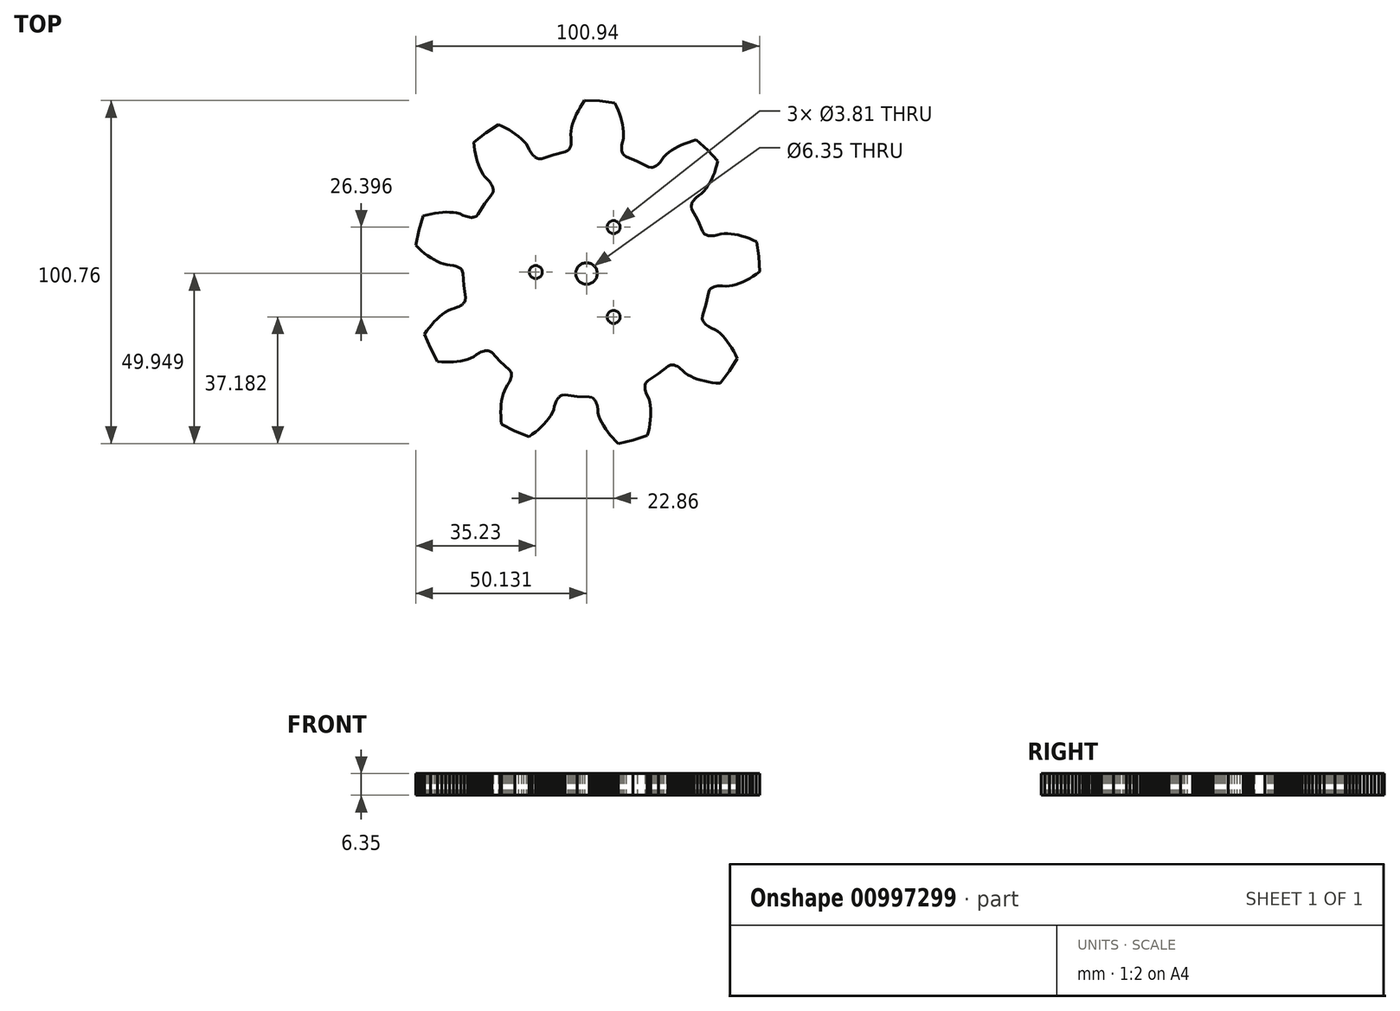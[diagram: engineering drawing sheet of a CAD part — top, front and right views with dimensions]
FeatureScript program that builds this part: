
annotation { "Feature Type Name" : "Feature", "Feature Type Description" : "" }
export const myFeature = defineFeature(function(context is Context, id is Id, definition is map)
    precondition{}
    {
        {
            var Q0;
            Q0=qCreatedBy(makeId("Top.planeOp"),FACE);
            var sketch = newSketch(context, id + "F0", { "sketchPlane" : qUnion([Q0])});
            skLineSegment(sketch, "E0", {"start": v(-36.57, -0.37) * mm, "end": v(-36.8, 0.44) * mm});
            skLineSegment(sketch, "E1", {"start": v(-36.8, 0.44) * mm, "end": v(-37.04, 0.75) * mm});
            skLineSegment(sketch, "E2", {"start": v(-37.04, 0.75) * mm, "end": v(-37.27, 0.98) * mm});
            skLineSegment(sketch, "E3", {"start": v(-37.27, 0.98) * mm, "end": v(-37.51, 1.17) * mm});
            skLineSegment(sketch, "E4", {"start": v(-37.51, 1.17) * mm, "end": v(-37.75, 1.32) * mm});
            skLineSegment(sketch, "E5", {"start": v(-37.75, 1.32) * mm, "end": v(-37.98, 1.45) * mm});
            skLineSegment(sketch, "E6", {"start": v(-37.98, 1.45) * mm, "end": v(-38.46, 1.66) * mm});
            skLineSegment(sketch, "E7", {"start": v(-38.46, 1.66) * mm, "end": v(-38.94, 1.82) * mm});
            skLineSegment(sketch, "E8", {"start": v(-38.94, 1.82) * mm, "end": v(-39.42, 1.93) * mm});
            skLineSegment(sketch, "E9", {"start": v(-39.42, 1.93) * mm, "end": v(-40.38, 2.07) * mm});
            skLineSegment(sketch, "E10", {"start": v(-40.38, 2.07) * mm, "end": v(-41.35, 2.12) * mm});
            skLineSegment(sketch, "E11", {"start": v(-41.35, 2.12) * mm, "end": v(-42.31, 2.36) * mm});
            skLineSegment(sketch, "E12", {"start": v(-42.31, 2.36) * mm, "end": v(-43.26, 2.7) * mm});
            skLineSegment(sketch, "E13", {"start": v(-43.26, 2.7) * mm, "end": v(-44.2, 3.13) * mm});
            skLineSegment(sketch, "E14", {"start": v(-44.2, 3.13) * mm, "end": v(-45.14, 3.63) * mm});
            skLineSegment(sketch, "E15", {"start": v(-45.14, 3.63) * mm, "end": v(-46.06, 4.2) * mm});
            skLineSegment(sketch, "E16", {"start": v(-46.06, 4.2) * mm, "end": v(-46.97, 4.81) * mm});
            skLineSegment(sketch, "E17", {"start": v(-46.97, 4.81) * mm, "end": v(-47.87, 5.5) * mm});
            skLineSegment(sketch, "E18", {"start": v(-47.87, 5.5) * mm, "end": v(-48.75, 6.23) * mm});
            skLineSegment(sketch, "E19", {"start": v(-48.75, 6.23) * mm, "end": v(-49.62, 7.02) * mm});
            skLineSegment(sketch, "E20", {"start": v(-49.62, 7.02) * mm, "end": v(-50.47, 7.86) * mm});
            skLineSegment(sketch, "E21", {"start": v(-50.47, 7.86) * mm, "end": v(-49.56, 12.2) * mm});
            skLineSegment(sketch, "E22", {"start": v(-49.56, 12.2) * mm, "end": v(-48.26, 16.46) * mm});
            skLineSegment(sketch, "E23", {"start": v(-48.26, 16.46) * mm, "end": v(-47.11, 16.78) * mm});
            skLineSegment(sketch, "E24", {"start": v(-47.11, 16.78) * mm, "end": v(-45.97, 17.06) * mm});
            skLineSegment(sketch, "E25", {"start": v(-45.97, 17.06) * mm, "end": v(-44.84, 17.27) * mm});
            skLineSegment(sketch, "E26", {"start": v(-44.84, 17.27) * mm, "end": v(-43.73, 17.44) * mm});
            skLineSegment(sketch, "E27", {"start": v(-43.73, 17.44) * mm, "end": v(-42.63, 17.54) * mm});
            skLineSegment(sketch, "E28", {"start": v(-42.63, 17.54) * mm, "end": v(-41.55, 17.6) * mm});
            skLineSegment(sketch, "E29", {"start": v(-41.55, 17.6) * mm, "end": v(-40.5, 17.58) * mm});
            skLineSegment(sketch, "E30", {"start": v(-40.5, 17.58) * mm, "end": v(-39.46, 17.5) * mm});
            skLineSegment(sketch, "E31", {"start": v(-39.46, 17.5) * mm, "end": v(-38.46, 17.34) * mm});
            skLineSegment(sketch, "E32", {"start": v(-38.46, 17.34) * mm, "end": v(-37.51, 17.09) * mm});
            skLineSegment(sketch, "E33", {"start": v(-37.51, 17.09) * mm, "end": v(-36.63, 16.67) * mm});
            skLineSegment(sketch, "E34", {"start": v(-36.63, 16.67) * mm, "end": v(-35.72, 16.33) * mm});
            skLineSegment(sketch, "E35", {"start": v(-35.72, 16.33) * mm, "end": v(-35.25, 16.2) * mm});
            skLineSegment(sketch, "E36", {"start": v(-35.25, 16.2) * mm, "end": v(-34.75, 16.1) * mm});
            skLineSegment(sketch, "E37", {"start": v(-34.75, 16.1) * mm, "end": v(-34.23, 16.06) * mm});
            skLineSegment(sketch, "E38", {"start": v(-34.23, 16.06) * mm, "end": v(-33.96, 16.05) * mm});
            skLineSegment(sketch, "E39", {"start": v(-33.96, 16.05) * mm, "end": v(-33.68, 16.08) * mm});
            skLineSegment(sketch, "E40", {"start": v(-33.68, 16.08) * mm, "end": v(-33.39, 16.12) * mm});
            skLineSegment(sketch, "E41", {"start": v(-33.39, 16.12) * mm, "end": v(-33.07, 16.21) * mm});
            skLineSegment(sketch, "E42", {"start": v(-33.07, 16.21) * mm, "end": v(-32.71, 16.38) * mm});
            skLineSegment(sketch, "E43", {"start": v(-32.71, 16.38) * mm, "end": v(-32.12, 16.97) * mm});
            skLineSegment(sketch, "E44", {"start": v(-32.12, 16.97) * mm, "end": v(-30.24, 20.04) * mm});
            skLineSegment(sketch, "E45", {"start": v(-30.24, 20.04) * mm, "end": v(-28.05, 22.9) * mm});
            skLineSegment(sketch, "E46", {"start": v(-28.05, 22.9) * mm, "end": v(-27.72, 23.67) * mm});
            skLineSegment(sketch, "E47", {"start": v(-27.72, 23.67) * mm, "end": v(-27.7, 24.07) * mm});
            skLineSegment(sketch, "E48", {"start": v(-27.7, 24.07) * mm, "end": v(-27.72, 24.4) * mm});
            skLineSegment(sketch, "E49", {"start": v(-27.72, 24.4) * mm, "end": v(-27.79, 24.69) * mm});
            skLineSegment(sketch, "E50", {"start": v(-27.79, 24.69) * mm, "end": v(-27.87, 24.96) * mm});
            skLineSegment(sketch, "E51", {"start": v(-27.87, 24.96) * mm, "end": v(-27.97, 25.2) * mm});
            skLineSegment(sketch, "E52", {"start": v(-27.97, 25.2) * mm, "end": v(-28.2, 25.67) * mm});
            skLineSegment(sketch, "E53", {"start": v(-28.2, 25.67) * mm, "end": v(-28.46, 26.1) * mm});
            skLineSegment(sketch, "E54", {"start": v(-28.46, 26.1) * mm, "end": v(-28.76, 26.5) * mm});
            skLineSegment(sketch, "E55", {"start": v(-28.76, 26.5) * mm, "end": v(-29.4, 27.22) * mm});
            skLineSegment(sketch, "E56", {"start": v(-29.4, 27.22) * mm, "end": v(-30.12, 27.89) * mm});
            skLineSegment(sketch, "E57", {"start": v(-30.12, 27.89) * mm, "end": v(-30.7, 28.69) * mm});
            skLineSegment(sketch, "E58", {"start": v(-30.7, 28.69) * mm, "end": v(-31.2, 29.56) * mm});
            skLineSegment(sketch, "E59", {"start": v(-31.2, 29.56) * mm, "end": v(-31.65, 30.5) * mm});
            skLineSegment(sketch, "E60", {"start": v(-31.65, 30.5) * mm, "end": v(-32.05, 31.47) * mm});
            skLineSegment(sketch, "E61", {"start": v(-32.05, 31.47) * mm, "end": v(-32.4, 32.5) * mm});
            skLineSegment(sketch, "E62", {"start": v(-32.4, 32.5) * mm, "end": v(-32.69, 33.56) * mm});
            skLineSegment(sketch, "E63", {"start": v(-32.69, 33.56) * mm, "end": v(-32.94, 34.66) * mm});
            skLineSegment(sketch, "E64", {"start": v(-32.94, 34.66) * mm, "end": v(-33.14, 35.8) * mm});
            skLineSegment(sketch, "E65", {"start": v(-33.14, 35.8) * mm, "end": v(-33.3, 36.95) * mm});
            skLineSegment(sketch, "E66", {"start": v(-33.3, 36.95) * mm, "end": v(-33.41, 38.14) * mm});
            skLineSegment(sketch, "E67", {"start": v(-33.41, 38.14) * mm, "end": v(-29.92, 40.88) * mm});
            skLineSegment(sketch, "E68", {"start": v(-29.92, 40.88) * mm, "end": v(-26.2, 43.31) * mm});
            skLineSegment(sketch, "E69", {"start": v(-26.2, 43.31) * mm, "end": v(-25.1, 42.82) * mm});
            skLineSegment(sketch, "E70", {"start": v(-25.1, 42.82) * mm, "end": v(-24.06, 42.3) * mm});
            skLineSegment(sketch, "E71", {"start": v(-24.06, 42.3) * mm, "end": v(-23.05, 41.74) * mm});
            skLineSegment(sketch, "E72", {"start": v(-23.05, 41.74) * mm, "end": v(-22.1, 41.15) * mm});
            skLineSegment(sketch, "E73", {"start": v(-22.1, 41.15) * mm, "end": v(-21.18, 40.52) * mm});
            skLineSegment(sketch, "E74", {"start": v(-21.18, 40.52) * mm, "end": v(-20.32, 39.87) * mm});
            skLineSegment(sketch, "E75", {"start": v(-20.32, 39.87) * mm, "end": v(-19.52, 39.18) * mm});
            skLineSegment(sketch, "E76", {"start": v(-19.52, 39.18) * mm, "end": v(-18.78, 38.45) * mm});
            skLineSegment(sketch, "E77", {"start": v(-18.78, 38.45) * mm, "end": v(-18.12, 37.7) * mm});
            skLineSegment(sketch, "E78", {"start": v(-18.12, 37.7) * mm, "end": v(-17.55, 36.88) * mm});
            skLineSegment(sketch, "E79", {"start": v(-17.55, 36.88) * mm, "end": v(-17.15, 36) * mm});
            skLineSegment(sketch, "E80", {"start": v(-17.15, 36) * mm, "end": v(-16.67, 35.15) * mm});
            skLineSegment(sketch, "E81", {"start": v(-16.67, 35.15) * mm, "end": v(-16.4, 34.74) * mm});
            skLineSegment(sketch, "E82", {"start": v(-16.4, 34.74) * mm, "end": v(-16.07, 34.35) * mm});
            skLineSegment(sketch, "E83", {"start": v(-16.07, 34.35) * mm, "end": v(-15.7, 33.99) * mm});
            skLineSegment(sketch, "E84", {"start": v(-15.7, 33.99) * mm, "end": v(-15.5, 33.81) * mm});
            skLineSegment(sketch, "E85", {"start": v(-15.5, 33.81) * mm, "end": v(-15.27, 33.65) * mm});
            skLineSegment(sketch, "E86", {"start": v(-15.27, 33.65) * mm, "end": v(-15.02, 33.5) * mm});
            skLineSegment(sketch, "E87", {"start": v(-15.02, 33.5) * mm, "end": v(-14.72, 33.36) * mm});
            skLineSegment(sketch, "E88", {"start": v(-14.72, 33.36) * mm, "end": v(-14.34, 33.25) * mm});
            skLineSegment(sketch, "E89", {"start": v(-14.34, 33.25) * mm, "end": v(-13.5, 33.33) * mm});
            skLineSegment(sketch, "E90", {"start": v(-13.5, 33.33) * mm, "end": v(-10.08, 34.47) * mm});
            skLineSegment(sketch, "E91", {"start": v(-10.08, 34.47) * mm, "end": v(-6.57, 35.26) * mm});
            skLineSegment(sketch, "E92", {"start": v(-6.57, 35.26) * mm, "end": v(-5.82, 35.63) * mm});
            skLineSegment(sketch, "E93", {"start": v(-5.82, 35.63) * mm, "end": v(-5.55, 35.92) * mm});
            skLineSegment(sketch, "E94", {"start": v(-5.55, 35.92) * mm, "end": v(-5.36, 36.19) * mm});
            skLineSegment(sketch, "E95", {"start": v(-5.36, 36.19) * mm, "end": v(-5.22, 36.45) * mm});
            skLineSegment(sketch, "E96", {"start": v(-5.22, 36.45) * mm, "end": v(-5.1, 36.71) * mm});
            skLineSegment(sketch, "E97", {"start": v(-5.1, 36.71) * mm, "end": v(-5.02, 36.97) * mm});
            skLineSegment(sketch, "E98", {"start": v(-5.02, 36.97) * mm, "end": v(-4.9, 37.47) * mm});
            skLineSegment(sketch, "E99", {"start": v(-4.9, 37.47) * mm, "end": v(-4.83, 37.97) * mm});
            skLineSegment(sketch, "E100", {"start": v(-4.83, 37.97) * mm, "end": v(-4.8, 38.46) * mm});
            skLineSegment(sketch, "E101", {"start": v(-4.8, 38.46) * mm, "end": v(-4.83, 39.44) * mm});
            skLineSegment(sketch, "E102", {"start": v(-4.83, 39.44) * mm, "end": v(-4.95, 40.4) * mm});
            skLineSegment(sketch, "E103", {"start": v(-4.95, 40.4) * mm, "end": v(-4.88, 41.39) * mm});
            skLineSegment(sketch, "E104", {"start": v(-4.88, 41.39) * mm, "end": v(-4.7, 42.38) * mm});
            skLineSegment(sketch, "E105", {"start": v(-4.7, 42.38) * mm, "end": v(-4.45, 43.39) * mm});
            skLineSegment(sketch, "E106", {"start": v(-4.45, 43.39) * mm, "end": v(-4.12, 44.4) * mm});
            skLineSegment(sketch, "E107", {"start": v(-4.12, 44.4) * mm, "end": v(-3.73, 45.4) * mm});
            skLineSegment(sketch, "E108", {"start": v(-3.73, 45.4) * mm, "end": v(-3.27, 46.4) * mm});
            skLineSegment(sketch, "E109", {"start": v(-3.27, 46.4) * mm, "end": v(-2.76, 47.4) * mm});
            skLineSegment(sketch, "E110", {"start": v(-2.76, 47.4) * mm, "end": v(-2.19, 48.4) * mm});
            skLineSegment(sketch, "E111", {"start": v(-2.19, 48.4) * mm, "end": v(-1.56, 49.4) * mm});
            skLineSegment(sketch, "E112", {"start": v(-1.56, 49.4) * mm, "end": v(-0.88, 50.38) * mm});
            skLineSegment(sketch, "E113", {"start": v(-0.88, 50.38) * mm, "end": v(3.56, 50.23) * mm});
            skLineSegment(sketch, "E114", {"start": v(3.56, 50.23) * mm, "end": v(7.97, 49.7) * mm});
            skLineSegment(sketch, "E115", {"start": v(7.97, 49.7) * mm, "end": v(8.5, 48.62) * mm});
            skLineSegment(sketch, "E116", {"start": v(8.5, 48.62) * mm, "end": v(8.96, 47.55) * mm});
            skLineSegment(sketch, "E117", {"start": v(8.96, 47.55) * mm, "end": v(9.37, 46.47) * mm});
            skLineSegment(sketch, "E118", {"start": v(9.37, 46.47) * mm, "end": v(9.72, 45.4) * mm});
            skLineSegment(sketch, "E119", {"start": v(9.72, 45.4) * mm, "end": v(10.02, 44.34) * mm});
            skLineSegment(sketch, "E120", {"start": v(10.02, 44.34) * mm, "end": v(10.25, 43.28) * mm});
            skLineSegment(sketch, "E121", {"start": v(10.25, 43.28) * mm, "end": v(10.43, 42.24) * mm});
            skLineSegment(sketch, "E122", {"start": v(10.43, 42.24) * mm, "end": v(10.53, 41.21) * mm});
            skLineSegment(sketch, "E123", {"start": v(10.53, 41.21) * mm, "end": v(10.55, 40.2) * mm});
            skLineSegment(sketch, "E124", {"start": v(10.55, 40.2) * mm, "end": v(10.46, 39.22) * mm});
            skLineSegment(sketch, "E125", {"start": v(10.46, 39.22) * mm, "end": v(10.2, 38.28) * mm});
            skLineSegment(sketch, "E126", {"start": v(10.2, 38.28) * mm, "end": v(10.02, 37.32) * mm});
            skLineSegment(sketch, "E127", {"start": v(10.02, 37.32) * mm, "end": v(9.97, 36.83) * mm});
            skLineSegment(sketch, "E128", {"start": v(9.97, 36.83) * mm, "end": v(9.97, 36.33) * mm});
            skLineSegment(sketch, "E129", {"start": v(9.97, 36.33) * mm, "end": v(10.01, 35.81) * mm});
            skLineSegment(sketch, "E130", {"start": v(10.01, 35.81) * mm, "end": v(10.06, 35.55) * mm});
            skLineSegment(sketch, "E131", {"start": v(10.06, 35.55) * mm, "end": v(10.13, 35.27) * mm});
            skLineSegment(sketch, "E132", {"start": v(10.13, 35.27) * mm, "end": v(10.22, 35) * mm});
            skLineSegment(sketch, "E133", {"start": v(10.22, 35) * mm, "end": v(10.37, 34.7) * mm});
            skLineSegment(sketch, "E134", {"start": v(10.37, 34.7) * mm, "end": v(10.6, 34.37) * mm});
            skLineSegment(sketch, "E135", {"start": v(10.6, 34.37) * mm, "end": v(11.28, 33.9) * mm});
            skLineSegment(sketch, "E136", {"start": v(11.28, 33.9) * mm, "end": v(14.63, 32.57) * mm});
            skLineSegment(sketch, "E137", {"start": v(14.63, 32.57) * mm, "end": v(17.83, 30.92) * mm});
            skLineSegment(sketch, "E138", {"start": v(17.83, 30.92) * mm, "end": v(18.65, 30.72) * mm});
            skLineSegment(sketch, "E139", {"start": v(18.65, 30.72) * mm, "end": v(19.04, 30.76) * mm});
            skLineSegment(sketch, "E140", {"start": v(19.04, 30.76) * mm, "end": v(19.35, 30.85) * mm});
            skLineSegment(sketch, "E141", {"start": v(19.35, 30.85) * mm, "end": v(19.63, 30.96) * mm});
            skLineSegment(sketch, "E142", {"start": v(19.63, 30.96) * mm, "end": v(19.88, 31.09) * mm});
            skLineSegment(sketch, "E143", {"start": v(19.88, 31.09) * mm, "end": v(20.11, 31.23) * mm});
            skLineSegment(sketch, "E144", {"start": v(20.11, 31.23) * mm, "end": v(20.53, 31.54) * mm});
            skLineSegment(sketch, "E145", {"start": v(20.53, 31.54) * mm, "end": v(20.9, 31.87) * mm});
            skLineSegment(sketch, "E146", {"start": v(20.9, 31.87) * mm, "end": v(21.25, 32.23) * mm});
            skLineSegment(sketch, "E147", {"start": v(21.25, 32.23) * mm, "end": v(21.85, 33) * mm});
            skLineSegment(sketch, "E148", {"start": v(21.85, 33) * mm, "end": v(22.38, 33.81) * mm});
            skLineSegment(sketch, "E149", {"start": v(22.38, 33.81) * mm, "end": v(23.06, 34.52) * mm});
            skLineSegment(sketch, "E150", {"start": v(23.06, 34.52) * mm, "end": v(23.84, 35.17) * mm});
            skLineSegment(sketch, "E151", {"start": v(23.84, 35.17) * mm, "end": v(24.68, 35.78) * mm});
            skLineSegment(sketch, "E152", {"start": v(24.68, 35.78) * mm, "end": v(25.58, 36.33) * mm});
            skLineSegment(sketch, "E153", {"start": v(25.58, 36.33) * mm, "end": v(26.52, 36.85) * mm});
            skLineSegment(sketch, "E154", {"start": v(26.52, 36.85) * mm, "end": v(27.52, 37.33) * mm});
            skLineSegment(sketch, "E155", {"start": v(27.52, 37.33) * mm, "end": v(28.56, 37.77) * mm});
            skLineSegment(sketch, "E156", {"start": v(28.56, 37.77) * mm, "end": v(29.64, 38.17) * mm});
            skLineSegment(sketch, "E157", {"start": v(29.64, 38.17) * mm, "end": v(30.75, 38.52) * mm});
            skLineSegment(sketch, "E158", {"start": v(30.75, 38.52) * mm, "end": v(31.9, 38.84) * mm});
            skLineSegment(sketch, "E159", {"start": v(31.9, 38.84) * mm, "end": v(35.21, 35.87) * mm});
            skLineSegment(sketch, "E160", {"start": v(35.21, 35.87) * mm, "end": v(38.25, 32.63) * mm});
            skLineSegment(sketch, "E161", {"start": v(38.25, 32.63) * mm, "end": v(37.96, 31.47) * mm});
            skLineSegment(sketch, "E162", {"start": v(37.96, 31.47) * mm, "end": v(37.62, 30.35) * mm});
            skLineSegment(sketch, "E163", {"start": v(37.62, 30.35) * mm, "end": v(37.25, 29.26) * mm});
            skLineSegment(sketch, "E164", {"start": v(37.25, 29.26) * mm, "end": v(36.83, 28.21) * mm});
            skLineSegment(sketch, "E165", {"start": v(36.83, 28.21) * mm, "end": v(36.37, 27.2) * mm});
            skLineSegment(sketch, "E166", {"start": v(36.37, 27.2) * mm, "end": v(35.88, 26.25) * mm});
            skLineSegment(sketch, "E167", {"start": v(35.88, 26.25) * mm, "end": v(35.34, 25.34) * mm});
            skLineSegment(sketch, "E168", {"start": v(35.34, 25.34) * mm, "end": v(34.75, 24.49) * mm});
            skLineSegment(sketch, "E169", {"start": v(34.75, 24.49) * mm, "end": v(34.12, 23.7) * mm});
            skLineSegment(sketch, "E170", {"start": v(34.12, 23.7) * mm, "end": v(33.42, 23) * mm});
            skLineSegment(sketch, "E171", {"start": v(33.42, 23) * mm, "end": v(32.62, 22.45) * mm});
            skLineSegment(sketch, "E172", {"start": v(32.62, 22.45) * mm, "end": v(31.86, 21.83) * mm});
            skLineSegment(sketch, "E173", {"start": v(31.86, 21.83) * mm, "end": v(31.51, 21.49) * mm});
            skLineSegment(sketch, "E174", {"start": v(31.51, 21.49) * mm, "end": v(31.19, 21.1) * mm});
            skLineSegment(sketch, "E175", {"start": v(31.19, 21.1) * mm, "end": v(30.89, 20.68) * mm});
            skLineSegment(sketch, "E176", {"start": v(30.89, 20.68) * mm, "end": v(30.75, 20.45) * mm});
            skLineSegment(sketch, "E177", {"start": v(30.75, 20.45) * mm, "end": v(30.63, 20.2) * mm});
            skLineSegment(sketch, "E178", {"start": v(30.63, 20.2) * mm, "end": v(30.52, 19.91) * mm});
            skLineSegment(sketch, "E179", {"start": v(30.52, 19.91) * mm, "end": v(30.44, 19.6) * mm});
            skLineSegment(sketch, "E180", {"start": v(30.44, 19.6) * mm, "end": v(30.4, 19.2) * mm});
            skLineSegment(sketch, "E181", {"start": v(30.4, 19.2) * mm, "end": v(30.62, 18.4) * mm});
            skLineSegment(sketch, "E182", {"start": v(30.62, 18.4) * mm, "end": v(32.34, 15.23) * mm});
            skLineSegment(sketch, "E183", {"start": v(32.34, 15.23) * mm, "end": v(33.73, 11.9) * mm});
            skLineSegment(sketch, "E184", {"start": v(33.73, 11.9) * mm, "end": v(34.23, 11.23) * mm});
            skLineSegment(sketch, "E185", {"start": v(34.23, 11.23) * mm, "end": v(34.55, 11) * mm});
            skLineSegment(sketch, "E186", {"start": v(34.55, 11) * mm, "end": v(34.85, 10.87) * mm});
            skLineSegment(sketch, "E187", {"start": v(34.85, 10.87) * mm, "end": v(35.14, 10.78) * mm});
            skLineSegment(sketch, "E188", {"start": v(35.14, 10.78) * mm, "end": v(35.41, 10.72) * mm});
            skLineSegment(sketch, "E189", {"start": v(35.41, 10.72) * mm, "end": v(35.68, 10.68) * mm});
            skLineSegment(sketch, "E190", {"start": v(35.68, 10.68) * mm, "end": v(36.2, 10.64) * mm});
            skLineSegment(sketch, "E191", {"start": v(36.2, 10.64) * mm, "end": v(36.7, 10.66) * mm});
            skLineSegment(sketch, "E192", {"start": v(36.7, 10.66) * mm, "end": v(37.2, 10.72) * mm});
            skLineSegment(sketch, "E193", {"start": v(37.2, 10.72) * mm, "end": v(38.14, 10.92) * mm});
            skLineSegment(sketch, "E194", {"start": v(38.14, 10.92) * mm, "end": v(39.08, 11.2) * mm});
            skLineSegment(sketch, "E195", {"start": v(39.08, 11.2) * mm, "end": v(40.06, 11.3) * mm});
            skLineSegment(sketch, "E196", {"start": v(40.06, 11.3) * mm, "end": v(41.07, 11.3) * mm});
            skLineSegment(sketch, "E197", {"start": v(41.07, 11.3) * mm, "end": v(42.1, 11.22) * mm});
            skLineSegment(sketch, "E198", {"start": v(42.1, 11.22) * mm, "end": v(43.15, 11.08) * mm});
            skLineSegment(sketch, "E199", {"start": v(43.15, 11.08) * mm, "end": v(44.2, 10.86) * mm});
            skLineSegment(sketch, "E200", {"start": v(44.2, 10.86) * mm, "end": v(45.27, 10.59) * mm});
            skLineSegment(sketch, "E201", {"start": v(45.27, 10.59) * mm, "end": v(46.35, 10.26) * mm});
            skLineSegment(sketch, "E202", {"start": v(46.35, 10.26) * mm, "end": v(47.43, 9.87) * mm});
            skLineSegment(sketch, "E203", {"start": v(47.43, 9.87) * mm, "end": v(48.52, 9.42) * mm});
            skLineSegment(sketch, "E204", {"start": v(48.52, 9.42) * mm, "end": v(49.6, 8.93) * mm});
            skLineSegment(sketch, "E205", {"start": v(49.6, 8.93) * mm, "end": v(50.23, 4.53) * mm});
            skLineSegment(sketch, "E206", {"start": v(50.23, 4.53) * mm, "end": v(50.47, 0.1) * mm});
            skLineSegment(sketch, "E207", {"start": v(50.47, 0.1) * mm, "end": v(49.5, -0.6) * mm});
            skLineSegment(sketch, "E208", {"start": v(49.5, -0.6) * mm, "end": v(48.52, -1.26) * mm});
            skLineSegment(sketch, "E209", {"start": v(48.52, -1.26) * mm, "end": v(47.54, -1.85) * mm});
            skLineSegment(sketch, "E210", {"start": v(47.54, -1.85) * mm, "end": v(46.55, -2.38) * mm});
            skLineSegment(sketch, "E211", {"start": v(46.55, -2.38) * mm, "end": v(45.55, -2.86) * mm});
            skLineSegment(sketch, "E212", {"start": v(45.55, -2.86) * mm, "end": v(44.55, -3.27) * mm});
            skLineSegment(sketch, "E213", {"start": v(44.55, -3.27) * mm, "end": v(43.55, -3.62) * mm});
            skLineSegment(sketch, "E214", {"start": v(43.55, -3.62) * mm, "end": v(42.56, -3.9) * mm});
            skLineSegment(sketch, "E215", {"start": v(42.56, -3.9) * mm, "end": v(41.57, -4.1) * mm});
            skLineSegment(sketch, "E216", {"start": v(41.57, -4.1) * mm, "end": v(40.58, -4.18) * mm});
            skLineSegment(sketch, "E217", {"start": v(40.58, -4.18) * mm, "end": v(39.62, -4.09) * mm});
            skLineSegment(sketch, "E218", {"start": v(39.62, -4.09) * mm, "end": v(38.64, -4.08) * mm});
            skLineSegment(sketch, "E219", {"start": v(38.64, -4.08) * mm, "end": v(38.15, -4.12) * mm});
            skLineSegment(sketch, "E220", {"start": v(38.15, -4.12) * mm, "end": v(37.65, -4.2) * mm});
            skLineSegment(sketch, "E221", {"start": v(37.65, -4.2) * mm, "end": v(37.15, -4.33) * mm});
            skLineSegment(sketch, "E222", {"start": v(37.15, -4.33) * mm, "end": v(36.9, -4.42) * mm});
            skLineSegment(sketch, "E223", {"start": v(36.9, -4.42) * mm, "end": v(36.64, -4.54) * mm});
            skLineSegment(sketch, "E224", {"start": v(36.64, -4.54) * mm, "end": v(36.38, -4.68) * mm});
            skLineSegment(sketch, "E225", {"start": v(36.38, -4.68) * mm, "end": v(36.11, -4.88) * mm});
            skLineSegment(sketch, "E226", {"start": v(36.11, -4.88) * mm, "end": v(35.83, -5.15) * mm});
            skLineSegment(sketch, "E227", {"start": v(35.83, -5.15) * mm, "end": v(35.48, -5.91) * mm});
            skLineSegment(sketch, "E228", {"start": v(35.48, -5.91) * mm, "end": v(34.76, -9.44) * mm});
            skLineSegment(sketch, "E229", {"start": v(34.76, -9.44) * mm, "end": v(33.69, -12.88) * mm});
            skLineSegment(sketch, "E230", {"start": v(33.69, -12.88) * mm, "end": v(33.63, -13.72) * mm});
            skLineSegment(sketch, "E231", {"start": v(33.63, -13.72) * mm, "end": v(33.74, -14.1) * mm});
            skLineSegment(sketch, "E232", {"start": v(33.74, -14.1) * mm, "end": v(33.89, -14.4) * mm});
            skLineSegment(sketch, "E233", {"start": v(33.89, -14.4) * mm, "end": v(34.04, -14.65) * mm});
            skLineSegment(sketch, "E234", {"start": v(34.04, -14.65) * mm, "end": v(34.21, -14.87) * mm});
            skLineSegment(sketch, "E235", {"start": v(34.21, -14.87) * mm, "end": v(34.4, -15.07) * mm});
            skLineSegment(sketch, "E236", {"start": v(34.4, -15.07) * mm, "end": v(34.77, -15.43) * mm});
            skLineSegment(sketch, "E237", {"start": v(34.77, -15.43) * mm, "end": v(35.16, -15.74) * mm});
            skLineSegment(sketch, "E238", {"start": v(35.16, -15.74) * mm, "end": v(35.57, -16.02) * mm});
            skLineSegment(sketch, "E239", {"start": v(35.57, -16.02) * mm, "end": v(36.44, -16.47) * mm});
            skLineSegment(sketch, "E240", {"start": v(36.44, -16.47) * mm, "end": v(37.33, -16.86) * mm});
            skLineSegment(sketch, "E241", {"start": v(37.33, -16.86) * mm, "end": v(38.15, -17.4) * mm});
            skLineSegment(sketch, "E242", {"start": v(38.15, -17.4) * mm, "end": v(38.92, -18.06) * mm});
            skLineSegment(sketch, "E243", {"start": v(38.92, -18.06) * mm, "end": v(39.66, -18.78) * mm});
            skLineSegment(sketch, "E244", {"start": v(39.66, -18.78) * mm, "end": v(40.37, -19.57) * mm});
            skLineSegment(sketch, "E245", {"start": v(40.37, -19.57) * mm, "end": v(41.04, -20.41) * mm});
            skLineSegment(sketch, "E246", {"start": v(41.04, -20.41) * mm, "end": v(41.69, -21.3) * mm});
            skLineSegment(sketch, "E247", {"start": v(41.69, -21.3) * mm, "end": v(42.3, -22.25) * mm});
            skLineSegment(sketch, "E248", {"start": v(42.3, -22.25) * mm, "end": v(42.88, -23.25) * mm});
            skLineSegment(sketch, "E249", {"start": v(42.88, -23.25) * mm, "end": v(43.42, -24.29) * mm});
            skLineSegment(sketch, "E250", {"start": v(43.42, -24.29) * mm, "end": v(43.93, -25.37) * mm});
            skLineSegment(sketch, "E251", {"start": v(43.93, -25.37) * mm, "end": v(41.59, -29.14) * mm});
            skLineSegment(sketch, "E252", {"start": v(41.59, -29.14) * mm, "end": v(38.92, -32.7) * mm});
            skLineSegment(sketch, "E253", {"start": v(38.92, -32.7) * mm, "end": v(37.73, -32.6) * mm});
            skLineSegment(sketch, "E254", {"start": v(37.73, -32.6) * mm, "end": v(36.56, -32.47) * mm});
            skLineSegment(sketch, "E255", {"start": v(36.56, -32.47) * mm, "end": v(35.43, -32.3) * mm});
            skLineSegment(sketch, "E256", {"start": v(35.43, -32.3) * mm, "end": v(34.32, -32.06) * mm});
            skLineSegment(sketch, "E257", {"start": v(34.32, -32.06) * mm, "end": v(33.25, -31.79) * mm});
            skLineSegment(sketch, "E258", {"start": v(33.25, -31.79) * mm, "end": v(32.22, -31.46) * mm});
            skLineSegment(sketch, "E259", {"start": v(32.22, -31.46) * mm, "end": v(31.23, -31.09) * mm});
            skLineSegment(sketch, "E260", {"start": v(31.23, -31.09) * mm, "end": v(30.3, -30.66) * mm});
            skLineSegment(sketch, "E261", {"start": v(30.3, -30.66) * mm, "end": v(29.4, -30.17) * mm});
            skLineSegment(sketch, "E262", {"start": v(29.4, -30.17) * mm, "end": v(28.6, -29.6) * mm});
            skLineSegment(sketch, "E263", {"start": v(28.6, -29.6) * mm, "end": v(27.92, -28.92) * mm});
            skLineSegment(sketch, "E264", {"start": v(27.92, -28.92) * mm, "end": v(27.18, -28.28) * mm});
            skLineSegment(sketch, "E265", {"start": v(27.18, -28.28) * mm, "end": v(26.78, -28) * mm});
            skLineSegment(sketch, "E266", {"start": v(26.78, -28) * mm, "end": v(26.34, -27.74) * mm});
            skLineSegment(sketch, "E267", {"start": v(26.34, -27.74) * mm, "end": v(25.87, -27.52) * mm});
            skLineSegment(sketch, "E268", {"start": v(25.87, -27.52) * mm, "end": v(25.62, -27.42) * mm});
            skLineSegment(sketch, "E269", {"start": v(25.62, -27.42) * mm, "end": v(25.35, -27.35) * mm});
            skLineSegment(sketch, "E270", {"start": v(25.35, -27.35) * mm, "end": v(25.06, -27.3) * mm});
            skLineSegment(sketch, "E271", {"start": v(25.06, -27.3) * mm, "end": v(24.73, -27.27) * mm});
            skLineSegment(sketch, "E272", {"start": v(24.73, -27.27) * mm, "end": v(24.33, -27.3) * mm});
            skLineSegment(sketch, "E273", {"start": v(24.33, -27.3) * mm, "end": v(23.58, -27.65) * mm});
            skLineSegment(sketch, "E274", {"start": v(23.58, -27.65) * mm, "end": v(20.75, -29.9) * mm});
            skLineSegment(sketch, "E275", {"start": v(20.75, -29.9) * mm, "end": v(17.72, -31.84) * mm});
            skLineSegment(sketch, "E276", {"start": v(17.72, -31.84) * mm, "end": v(17.14, -32.45) * mm});
            skLineSegment(sketch, "E277", {"start": v(17.14, -32.45) * mm, "end": v(16.99, -32.8) * mm});
            skLineSegment(sketch, "E278", {"start": v(16.99, -32.8) * mm, "end": v(16.9, -33.13) * mm});
            skLineSegment(sketch, "E279", {"start": v(16.9, -33.13) * mm, "end": v(16.86, -33.42) * mm});
            skLineSegment(sketch, "E280", {"start": v(16.86, -33.42) * mm, "end": v(16.85, -33.7) * mm});
            skLineSegment(sketch, "E281", {"start": v(16.85, -33.7) * mm, "end": v(16.85, -33.97) * mm});
            skLineSegment(sketch, "E282", {"start": v(16.85, -33.97) * mm, "end": v(16.91, -34.49) * mm});
            skLineSegment(sketch, "E283", {"start": v(16.91, -34.49) * mm, "end": v(17.01, -34.98) * mm});
            skLineSegment(sketch, "E284", {"start": v(17.01, -34.98) * mm, "end": v(17.15, -35.46) * mm});
            skLineSegment(sketch, "E285", {"start": v(17.15, -35.46) * mm, "end": v(17.52, -36.36) * mm});
            skLineSegment(sketch, "E286", {"start": v(17.52, -36.36) * mm, "end": v(17.96, -37.23) * mm});
            skLineSegment(sketch, "E287", {"start": v(17.96, -37.23) * mm, "end": v(18.23, -38.18) * mm});
            skLineSegment(sketch, "E288", {"start": v(18.23, -38.18) * mm, "end": v(18.4, -39.17) * mm});
            skLineSegment(sketch, "E289", {"start": v(18.4, -39.17) * mm, "end": v(18.5, -40.2) * mm});
            skLineSegment(sketch, "E290", {"start": v(18.5, -40.2) * mm, "end": v(18.54, -41.26) * mm});
            skLineSegment(sketch, "E291", {"start": v(18.54, -41.26) * mm, "end": v(18.52, -42.34) * mm});
            skLineSegment(sketch, "E292", {"start": v(18.52, -42.34) * mm, "end": v(18.43, -43.44) * mm});
            skLineSegment(sketch, "E293", {"start": v(18.43, -43.44) * mm, "end": v(18.3, -44.56) * mm});
            skLineSegment(sketch, "E294", {"start": v(18.3, -44.56) * mm, "end": v(18.1, -45.69) * mm});
            skLineSegment(sketch, "E295", {"start": v(18.1, -45.69) * mm, "end": v(17.85, -46.83) * mm});
            skLineSegment(sketch, "E296", {"start": v(17.85, -46.83) * mm, "end": v(17.55, -48) * mm});
            skLineSegment(sketch, "E297", {"start": v(17.55, -48) * mm, "end": v(13.33, -49.37) * mm});
            skLineSegment(sketch, "E298", {"start": v(13.33, -49.37) * mm, "end": v(9, -50.38) * mm});
            skLineSegment(sketch, "E299", {"start": v(9, -50.38) * mm, "end": v(8.14, -49.55) * mm});
            skLineSegment(sketch, "E300", {"start": v(8.14, -49.55) * mm, "end": v(7.33, -48.7) * mm});
            skLineSegment(sketch, "E301", {"start": v(7.33, -48.7) * mm, "end": v(6.58, -47.83) * mm});
            skLineSegment(sketch, "E302", {"start": v(6.58, -47.83) * mm, "end": v(5.88, -46.94) * mm});
            skLineSegment(sketch, "E303", {"start": v(5.88, -46.94) * mm, "end": v(5.24, -46.04) * mm});
            skLineSegment(sketch, "E304", {"start": v(5.24, -46.04) * mm, "end": v(4.66, -45.13) * mm});
            skLineSegment(sketch, "E305", {"start": v(4.66, -45.13) * mm, "end": v(4.14, -44.21) * mm});
            skLineSegment(sketch, "E306", {"start": v(4.14, -44.21) * mm, "end": v(3.7, -43.28) * mm});
            skLineSegment(sketch, "E307", {"start": v(3.7, -43.28) * mm, "end": v(3.33, -42.34) * mm});
            skLineSegment(sketch, "E308", {"start": v(3.33, -42.34) * mm, "end": v(3.07, -41.38) * mm});
            skLineSegment(sketch, "E309", {"start": v(3.07, -41.38) * mm, "end": v(3, -40.41) * mm});
            skLineSegment(sketch, "E310", {"start": v(3, -40.41) * mm, "end": v(2.84, -39.45) * mm});
            skLineSegment(sketch, "E311", {"start": v(2.84, -39.45) * mm, "end": v(2.72, -38.97) * mm});
            skLineSegment(sketch, "E312", {"start": v(2.72, -38.97) * mm, "end": v(2.55, -38.5) * mm});
            skLineSegment(sketch, "E313", {"start": v(2.55, -38.5) * mm, "end": v(2.33, -38.03) * mm});
            skLineSegment(sketch, "E314", {"start": v(2.33, -38.03) * mm, "end": v(2.2, -37.8) * mm});
            skLineSegment(sketch, "E315", {"start": v(2.2, -37.8) * mm, "end": v(2.04, -37.56) * mm});
            skLineSegment(sketch, "E316", {"start": v(2.04, -37.56) * mm, "end": v(1.85, -37.33) * mm});
            skLineSegment(sketch, "E317", {"start": v(1.85, -37.33) * mm, "end": v(1.61, -37.1) * mm});
            skLineSegment(sketch, "E318", {"start": v(1.61, -37.1) * mm, "end": v(1.3, -36.87) * mm});
            skLineSegment(sketch, "E319", {"start": v(1.3, -36.87) * mm, "end": v(0.48, -36.66) * mm});
            skLineSegment(sketch, "E320", {"start": v(0.48, -36.66) * mm, "end": v(-3.12, -36.56) * mm});
            skLineSegment(sketch, "E321", {"start": v(-3.12, -36.56) * mm, "end": v(-6.7, -36.1) * mm});
            skLineSegment(sketch, "E322", {"start": v(-6.7, -36.1) * mm, "end": v(-7.53, -36.2) * mm});
            skLineSegment(sketch, "E323", {"start": v(-7.53, -36.2) * mm, "end": v(-7.88, -36.37) * mm});
            skLineSegment(sketch, "E324", {"start": v(-7.88, -36.37) * mm, "end": v(-8.15, -36.56) * mm});
            skLineSegment(sketch, "E325", {"start": v(-8.15, -36.56) * mm, "end": v(-8.37, -36.76) * mm});
            skLineSegment(sketch, "E326", {"start": v(-8.37, -36.76) * mm, "end": v(-8.56, -36.97) * mm});
            skLineSegment(sketch, "E327", {"start": v(-8.56, -36.97) * mm, "end": v(-8.73, -37.18) * mm});
            skLineSegment(sketch, "E328", {"start": v(-8.73, -37.18) * mm, "end": v(-9.02, -37.6) * mm});
            skLineSegment(sketch, "E329", {"start": v(-9.02, -37.6) * mm, "end": v(-9.25, -38.05) * mm});
            skLineSegment(sketch, "E330", {"start": v(-9.25, -38.05) * mm, "end": v(-9.45, -38.5) * mm});
            skLineSegment(sketch, "E331", {"start": v(-9.45, -38.5) * mm, "end": v(-9.75, -39.43) * mm});
            skLineSegment(sketch, "E332", {"start": v(-9.75, -39.43) * mm, "end": v(-9.98, -40.38) * mm});
            skLineSegment(sketch, "E333", {"start": v(-9.98, -40.38) * mm, "end": v(-10.38, -41.28) * mm});
            skLineSegment(sketch, "E334", {"start": v(-10.38, -41.28) * mm, "end": v(-10.88, -42.16) * mm});
            skLineSegment(sketch, "E335", {"start": v(-10.88, -42.16) * mm, "end": v(-11.46, -43.01) * mm});
            skLineSegment(sketch, "E336", {"start": v(-11.46, -43.01) * mm, "end": v(-12.12, -43.84) * mm});
            skLineSegment(sketch, "E337", {"start": v(-12.12, -43.84) * mm, "end": v(-12.83, -44.65) * mm});
            skLineSegment(sketch, "E338", {"start": v(-12.83, -44.65) * mm, "end": v(-13.6, -45.44) * mm});
            skLineSegment(sketch, "E339", {"start": v(-13.6, -45.44) * mm, "end": v(-14.43, -46.2) * mm});
            skLineSegment(sketch, "E340", {"start": v(-14.43, -46.2) * mm, "end": v(-15.3, -46.95) * mm});
            skLineSegment(sketch, "E341", {"start": v(-15.3, -46.95) * mm, "end": v(-16.23, -47.67) * mm});
            skLineSegment(sketch, "E342", {"start": v(-16.23, -47.67) * mm, "end": v(-17.2, -48.36) * mm});
            skLineSegment(sketch, "E343", {"start": v(-17.2, -48.36) * mm, "end": v(-21.33, -46.7) * mm});
            skLineSegment(sketch, "E344", {"start": v(-21.33, -46.7) * mm, "end": v(-25.3, -44.7) * mm});
            skLineSegment(sketch, "E345", {"start": v(-25.3, -44.7) * mm, "end": v(-25.41, -43.5) * mm});
            skLineSegment(sketch, "E346", {"start": v(-25.41, -43.5) * mm, "end": v(-25.48, -42.33) * mm});
            skLineSegment(sketch, "E347", {"start": v(-25.48, -42.33) * mm, "end": v(-25.5, -41.19) * mm});
            skLineSegment(sketch, "E348", {"start": v(-25.5, -41.19) * mm, "end": v(-25.47, -40.06) * mm});
            skLineSegment(sketch, "E349", {"start": v(-25.47, -40.06) * mm, "end": v(-25.39, -38.96) * mm});
            skLineSegment(sketch, "E350", {"start": v(-25.39, -38.96) * mm, "end": v(-25.25, -37.89) * mm});
            skLineSegment(sketch, "E351", {"start": v(-25.25, -37.89) * mm, "end": v(-25.05, -36.85) * mm});
            skLineSegment(sketch, "E352", {"start": v(-25.05, -36.85) * mm, "end": v(-24.8, -35.85) * mm});
            skLineSegment(sketch, "E353", {"start": v(-24.8, -35.85) * mm, "end": v(-24.47, -34.9) * mm});
            skLineSegment(sketch, "E354", {"start": v(-24.47, -34.9) * mm, "end": v(-24.05, -34) * mm});
            skLineSegment(sketch, "E355", {"start": v(-24.05, -34) * mm, "end": v(-23.48, -33.2) * mm});
            skLineSegment(sketch, "E356", {"start": v(-23.48, -33.2) * mm, "end": v(-22.99, -32.37) * mm});
            skLineSegment(sketch, "E357", {"start": v(-22.99, -32.37) * mm, "end": v(-22.77, -31.92) * mm});
            skLineSegment(sketch, "E358", {"start": v(-22.77, -31.92) * mm, "end": v(-22.6, -31.45) * mm});
            skLineSegment(sketch, "E359", {"start": v(-22.6, -31.45) * mm, "end": v(-22.46, -30.95) * mm});
            skLineSegment(sketch, "E360", {"start": v(-22.46, -30.95) * mm, "end": v(-22.41, -30.68) * mm});
            skLineSegment(sketch, "E361", {"start": v(-22.41, -30.68) * mm, "end": v(-22.38, -30.4) * mm});
            skLineSegment(sketch, "E362", {"start": v(-22.38, -30.4) * mm, "end": v(-22.38, -30.1) * mm});
            skLineSegment(sketch, "E363", {"start": v(-22.38, -30.1) * mm, "end": v(-22.41, -29.78) * mm});
            skLineSegment(sketch, "E364", {"start": v(-22.41, -29.78) * mm, "end": v(-22.51, -29.4) * mm});
            skLineSegment(sketch, "E365", {"start": v(-22.51, -29.4) * mm, "end": v(-23, -28.71) * mm});
            skLineSegment(sketch, "E366", {"start": v(-23, -28.71) * mm, "end": v(-25.7, -26.32) * mm});
            skLineSegment(sketch, "E367", {"start": v(-25.7, -26.32) * mm, "end": v(-28.14, -23.67) * mm});
            skLineSegment(sketch, "E368", {"start": v(-28.14, -23.67) * mm, "end": v(-28.83, -23.2) * mm});
            skLineSegment(sketch, "E369", {"start": v(-28.83, -23.2) * mm, "end": v(-29.21, -23.11) * mm});
            skLineSegment(sketch, "E370", {"start": v(-29.21, -23.11) * mm, "end": v(-29.54, -23.09) * mm});
            skLineSegment(sketch, "E371", {"start": v(-29.54, -23.09) * mm, "end": v(-29.84, -23.1) * mm});
            skLineSegment(sketch, "E372", {"start": v(-29.84, -23.1) * mm, "end": v(-30.12, -23.13) * mm});
            skLineSegment(sketch, "E373", {"start": v(-30.12, -23.13) * mm, "end": v(-30.39, -23.19) * mm});
            skLineSegment(sketch, "E374", {"start": v(-30.39, -23.19) * mm, "end": v(-30.88, -23.33) * mm});
            skLineSegment(sketch, "E375", {"start": v(-30.88, -23.33) * mm, "end": v(-31.35, -23.52) * mm});
            skLineSegment(sketch, "E376", {"start": v(-31.35, -23.52) * mm, "end": v(-31.8, -23.74) * mm});
            skLineSegment(sketch, "E377", {"start": v(-31.8, -23.74) * mm, "end": v(-32.62, -24.26) * mm});
            skLineSegment(sketch, "E378", {"start": v(-32.62, -24.26) * mm, "end": v(-33.4, -24.84) * mm});
            skLineSegment(sketch, "E379", {"start": v(-33.4, -24.84) * mm, "end": v(-34.29, -25.27) * mm});
            skLineSegment(sketch, "E380", {"start": v(-34.29, -25.27) * mm, "end": v(-35.24, -25.62) * mm});
            skLineSegment(sketch, "E381", {"start": v(-35.24, -25.62) * mm, "end": v(-36.23, -25.9) * mm});
            skLineSegment(sketch, "E382", {"start": v(-36.23, -25.9) * mm, "end": v(-37.27, -26.12) * mm});
            skLineSegment(sketch, "E383", {"start": v(-37.27, -26.12) * mm, "end": v(-38.33, -26.28) * mm});
            skLineSegment(sketch, "E384", {"start": v(-38.33, -26.28) * mm, "end": v(-39.43, -26.39) * mm});
            skLineSegment(sketch, "E385", {"start": v(-39.43, -26.39) * mm, "end": v(-40.56, -26.44) * mm});
            skLineSegment(sketch, "E386", {"start": v(-40.56, -26.44) * mm, "end": v(-41.7, -26.45) * mm});
            skLineSegment(sketch, "E387", {"start": v(-41.7, -26.45) * mm, "end": v(-42.88, -26.4) * mm});
            skLineSegment(sketch, "E388", {"start": v(-42.88, -26.4) * mm, "end": v(-44.07, -26.3) * mm});
            skLineSegment(sketch, "E389", {"start": v(-44.07, -26.3) * mm, "end": v(-46.16, -22.39) * mm});
            skLineSegment(sketch, "E390", {"start": v(-46.16, -22.39) * mm, "end": v(-47.9, -18.3) * mm});
            skLineSegment(sketch, "E391", {"start": v(-47.9, -18.3) * mm, "end": v(-47.23, -17.31) * mm});
            skLineSegment(sketch, "E392", {"start": v(-47.23, -17.31) * mm, "end": v(-46.54, -16.37) * mm});
            skLineSegment(sketch, "E393", {"start": v(-46.54, -16.37) * mm, "end": v(-45.81, -15.48) * mm});
            skLineSegment(sketch, "E394", {"start": v(-45.81, -15.48) * mm, "end": v(-45.06, -14.63) * mm});
            skLineSegment(sketch, "E395", {"start": v(-45.06, -14.63) * mm, "end": v(-44.3, -13.85) * mm});
            skLineSegment(sketch, "E396", {"start": v(-44.3, -13.85) * mm, "end": v(-43.5, -13.11) * mm});
            skLineSegment(sketch, "E397", {"start": v(-43.5, -13.11) * mm, "end": v(-42.68, -12.45) * mm});
            skLineSegment(sketch, "E398", {"start": v(-42.68, -12.45) * mm, "end": v(-41.84, -11.84) * mm});
            skLineSegment(sketch, "E399", {"start": v(-41.84, -11.84) * mm, "end": v(-40.97, -11.32) * mm});
            skLineSegment(sketch, "E400", {"start": v(-40.97, -11.32) * mm, "end": v(-40.08, -10.9) * mm});
            skLineSegment(sketch, "E401", {"start": v(-40.08, -10.9) * mm, "end": v(-39.14, -10.66) * mm});
            skLineSegment(sketch, "E402", {"start": v(-39.14, -10.66) * mm, "end": v(-38.21, -10.34) * mm});
            skLineSegment(sketch, "E403", {"start": v(-38.21, -10.34) * mm, "end": v(-37.77, -10.13) * mm});
            skLineSegment(sketch, "E404", {"start": v(-37.77, -10.13) * mm, "end": v(-37.33, -9.89) * mm});
            skLineSegment(sketch, "E405", {"start": v(-37.33, -9.89) * mm, "end": v(-36.9, -9.59) * mm});
            skLineSegment(sketch, "E406", {"start": v(-36.9, -9.59) * mm, "end": v(-36.7, -9.42) * mm});
            skLineSegment(sketch, "E407", {"start": v(-36.7, -9.42) * mm, "end": v(-36.5, -9.22) * mm});
            skLineSegment(sketch, "E408", {"start": v(-36.5, -9.22) * mm, "end": v(-36.3, -9) * mm});
            skLineSegment(sketch, "E409", {"start": v(-36.3, -9) * mm, "end": v(-36.11, -8.72) * mm});
            skLineSegment(sketch, "E410", {"start": v(-36.11, -8.72) * mm, "end": v(-35.94, -8.37) * mm});
            skLineSegment(sketch, "E411", {"start": v(-35.94, -8.37) * mm, "end": v(-35.87, -7.53) * mm});
            skLineSegment(sketch, "E412", {"start": v(-35.87, -7.53) * mm, "end": v(-36.4, -3.97) * mm});
            skLineSegment(sketch, "E413", {"start": v(-36.4, -3.97) * mm, "end": v(-36.57, -0.37) * mm});
            skCircle(sketch, "E414", {"center": v(-0.34, -0.43) * mm, "radius": 3.18 * mm});
            skSolve(sketch);
        }
        {
            var Q0;
            Q0 = qSketchRegion(id + "F0", true);
            extrude(context, id + "F1", {"entities" : qUnion([Q0]), "depth" : 6.35 * mm, "offsetDistance" : 25.4 * mm});
        }
        {
            var Q0;
            Q0=makeQuery(id+"F1.opExtrude","CAP_FACE",FACE,{"disambiguationData":[OSD([sQuery(id+"F0.wireOp",EDGE,"E0"),sQuery(id+"F0.wireOp",EDGE,"E1"),sQuery(id+"F0.wireOp",EDGE,"E2"),sQuery(id+"F0.wireOp",EDGE,"E3"),sQuery(id+"F0.wireOp",EDGE,"E4"),sQuery(id+"F0.wireOp",EDGE,"E5"),sQuery(id+"F0.wireOp",EDGE,"E6"),sQuery(id+"F0.wireOp",EDGE,"E7"),sQuery(id+"F0.wireOp",EDGE,"E8"),sQuery(id+"F0.wireOp",EDGE,"E9"),sQuery(id+"F0.wireOp",EDGE,"E10"),sQuery(id+"F0.wireOp",EDGE,"E11"),sQuery(id+"F0.wireOp",EDGE,"E12"),sQuery(id+"F0.wireOp",EDGE,"E13"),sQuery(id+"F0.wireOp",EDGE,"E14"),sQuery(id+"F0.wireOp",EDGE,"E15"),sQuery(id+"F0.wireOp",EDGE,"E16"),sQuery(id+"F0.wireOp",EDGE,"E17"),sQuery(id+"F0.wireOp",EDGE,"E18"),sQuery(id+"F0.wireOp",EDGE,"E19"),sQuery(id+"F0.wireOp",EDGE,"E20"),sQuery(id+"F0.wireOp",EDGE,"E21"),sQuery(id+"F0.wireOp",EDGE,"E22"),sQuery(id+"F0.wireOp",EDGE,"E23"),sQuery(id+"F0.wireOp",EDGE,"E24"),sQuery(id+"F0.wireOp",EDGE,"E25"),sQuery(id+"F0.wireOp",EDGE,"E26"),sQuery(id+"F0.wireOp",EDGE,"E27"),sQuery(id+"F0.wireOp",EDGE,"E28"),sQuery(id+"F0.wireOp",EDGE,"E29"),sQuery(id+"F0.wireOp",EDGE,"E30"),sQuery(id+"F0.wireOp",EDGE,"E31"),sQuery(id+"F0.wireOp",EDGE,"E32"),sQuery(id+"F0.wireOp",EDGE,"E33"),sQuery(id+"F0.wireOp",EDGE,"E34"),sQuery(id+"F0.wireOp",EDGE,"E35"),sQuery(id+"F0.wireOp",EDGE,"E36"),sQuery(id+"F0.wireOp",EDGE,"E37"),sQuery(id+"F0.wireOp",EDGE,"E38"),sQuery(id+"F0.wireOp",EDGE,"E39"),sQuery(id+"F0.wireOp",EDGE,"E40"),sQuery(id+"F0.wireOp",EDGE,"E41"),sQuery(id+"F0.wireOp",EDGE,"E42"),sQuery(id+"F0.wireOp",EDGE,"E43"),sQuery(id+"F0.wireOp",EDGE,"E44"),sQuery(id+"F0.wireOp",EDGE,"E45"),sQuery(id+"F0.wireOp",EDGE,"E46"),sQuery(id+"F0.wireOp",EDGE,"E47"),sQuery(id+"F0.wireOp",EDGE,"E48"),sQuery(id+"F0.wireOp",EDGE,"E49"),sQuery(id+"F0.wireOp",EDGE,"E50"),sQuery(id+"F0.wireOp",EDGE,"E51"),sQuery(id+"F0.wireOp",EDGE,"E52"),sQuery(id+"F0.wireOp",EDGE,"E53"),sQuery(id+"F0.wireOp",EDGE,"E54"),sQuery(id+"F0.wireOp",EDGE,"E55"),sQuery(id+"F0.wireOp",EDGE,"E56"),sQuery(id+"F0.wireOp",EDGE,"E57"),sQuery(id+"F0.wireOp",EDGE,"E58"),sQuery(id+"F0.wireOp",EDGE,"E59"),sQuery(id+"F0.wireOp",EDGE,"E60"),sQuery(id+"F0.wireOp",EDGE,"E61"),sQuery(id+"F0.wireOp",EDGE,"E62"),sQuery(id+"F0.wireOp",EDGE,"E63"),sQuery(id+"F0.wireOp",EDGE,"E64"),sQuery(id+"F0.wireOp",EDGE,"E65"),sQuery(id+"F0.wireOp",EDGE,"E66"),sQuery(id+"F0.wireOp",EDGE,"E67"),sQuery(id+"F0.wireOp",EDGE,"E68"),sQuery(id+"F0.wireOp",EDGE,"E69"),sQuery(id+"F0.wireOp",EDGE,"E70"),sQuery(id+"F0.wireOp",EDGE,"E71"),sQuery(id+"F0.wireOp",EDGE,"E72"),sQuery(id+"F0.wireOp",EDGE,"E73"),sQuery(id+"F0.wireOp",EDGE,"E74"),sQuery(id+"F0.wireOp",EDGE,"E75"),sQuery(id+"F0.wireOp",EDGE,"E76"),sQuery(id+"F0.wireOp",EDGE,"E77"),sQuery(id+"F0.wireOp",EDGE,"E78"),sQuery(id+"F0.wireOp",EDGE,"E79"),sQuery(id+"F0.wireOp",EDGE,"E80"),sQuery(id+"F0.wireOp",EDGE,"E81"),sQuery(id+"F0.wireOp",EDGE,"E82"),sQuery(id+"F0.wireOp",EDGE,"E83"),sQuery(id+"F0.wireOp",EDGE,"E84"),sQuery(id+"F0.wireOp",EDGE,"E85"),sQuery(id+"F0.wireOp",EDGE,"E86"),sQuery(id+"F0.wireOp",EDGE,"E87"),sQuery(id+"F0.wireOp",EDGE,"E88"),sQuery(id+"F0.wireOp",EDGE,"E89"),sQuery(id+"F0.wireOp",EDGE,"E90"),sQuery(id+"F0.wireOp",EDGE,"E91"),sQuery(id+"F0.wireOp",EDGE,"E92"),sQuery(id+"F0.wireOp",EDGE,"E93"),sQuery(id+"F0.wireOp",EDGE,"E94"),sQuery(id+"F0.wireOp",EDGE,"E95"),sQuery(id+"F0.wireOp",EDGE,"E96"),sQuery(id+"F0.wireOp",EDGE,"E97"),sQuery(id+"F0.wireOp",EDGE,"E98"),sQuery(id+"F0.wireOp",EDGE,"E99"),sQuery(id+"F0.wireOp",EDGE,"E100"),sQuery(id+"F0.wireOp",EDGE,"E101"),sQuery(id+"F0.wireOp",EDGE,"E102"),sQuery(id+"F0.wireOp",EDGE,"E103"),sQuery(id+"F0.wireOp",EDGE,"E104"),sQuery(id+"F0.wireOp",EDGE,"E105"),sQuery(id+"F0.wireOp",EDGE,"E106"),sQuery(id+"F0.wireOp",EDGE,"E107"),sQuery(id+"F0.wireOp",EDGE,"E108"),sQuery(id+"F0.wireOp",EDGE,"E109"),sQuery(id+"F0.wireOp",EDGE,"E110"),sQuery(id+"F0.wireOp",EDGE,"E111"),sQuery(id+"F0.wireOp",EDGE,"E112"),sQuery(id+"F0.wireOp",EDGE,"E113"),sQuery(id+"F0.wireOp",EDGE,"E114"),sQuery(id+"F0.wireOp",EDGE,"E115"),sQuery(id+"F0.wireOp",EDGE,"E116"),sQuery(id+"F0.wireOp",EDGE,"E117"),sQuery(id+"F0.wireOp",EDGE,"E118"),sQuery(id+"F0.wireOp",EDGE,"E119"),sQuery(id+"F0.wireOp",EDGE,"E120"),sQuery(id+"F0.wireOp",EDGE,"E121"),sQuery(id+"F0.wireOp",EDGE,"E122"),sQuery(id+"F0.wireOp",EDGE,"E123"),sQuery(id+"F0.wireOp",EDGE,"E124"),sQuery(id+"F0.wireOp",EDGE,"E125"),sQuery(id+"F0.wireOp",EDGE,"E126"),sQuery(id+"F0.wireOp",EDGE,"E127"),sQuery(id+"F0.wireOp",EDGE,"E128"),sQuery(id+"F0.wireOp",EDGE,"E129"),sQuery(id+"F0.wireOp",EDGE,"E130"),sQuery(id+"F0.wireOp",EDGE,"E131"),sQuery(id+"F0.wireOp",EDGE,"E132"),sQuery(id+"F0.wireOp",EDGE,"E133"),sQuery(id+"F0.wireOp",EDGE,"E134"),sQuery(id+"F0.wireOp",EDGE,"E135"),sQuery(id+"F0.wireOp",EDGE,"E136"),sQuery(id+"F0.wireOp",EDGE,"E137"),sQuery(id+"F0.wireOp",EDGE,"E138"),sQuery(id+"F0.wireOp",EDGE,"E139"),sQuery(id+"F0.wireOp",EDGE,"E140"),sQuery(id+"F0.wireOp",EDGE,"E141"),sQuery(id+"F0.wireOp",EDGE,"E142"),sQuery(id+"F0.wireOp",EDGE,"E143"),sQuery(id+"F0.wireOp",EDGE,"E144"),sQuery(id+"F0.wireOp",EDGE,"E145"),sQuery(id+"F0.wireOp",EDGE,"E146"),sQuery(id+"F0.wireOp",EDGE,"E147"),sQuery(id+"F0.wireOp",EDGE,"E148"),sQuery(id+"F0.wireOp",EDGE,"E149"),sQuery(id+"F0.wireOp",EDGE,"E150"),sQuery(id+"F0.wireOp",EDGE,"E151"),sQuery(id+"F0.wireOp",EDGE,"E152"),sQuery(id+"F0.wireOp",EDGE,"E153"),sQuery(id+"F0.wireOp",EDGE,"E154"),sQuery(id+"F0.wireOp",EDGE,"E155"),sQuery(id+"F0.wireOp",EDGE,"E156"),sQuery(id+"F0.wireOp",EDGE,"E157"),sQuery(id+"F0.wireOp",EDGE,"E158"),sQuery(id+"F0.wireOp",EDGE,"E159"),sQuery(id+"F0.wireOp",EDGE,"E160"),sQuery(id+"F0.wireOp",EDGE,"E161"),sQuery(id+"F0.wireOp",EDGE,"E162"),sQuery(id+"F0.wireOp",EDGE,"E163"),sQuery(id+"F0.wireOp",EDGE,"E164"),sQuery(id+"F0.wireOp",EDGE,"E165"),sQuery(id+"F0.wireOp",EDGE,"E166"),sQuery(id+"F0.wireOp",EDGE,"E167"),sQuery(id+"F0.wireOp",EDGE,"E168"),sQuery(id+"F0.wireOp",EDGE,"E169"),sQuery(id+"F0.wireOp",EDGE,"E170"),sQuery(id+"F0.wireOp",EDGE,"E171"),sQuery(id+"F0.wireOp",EDGE,"E172"),sQuery(id+"F0.wireOp",EDGE,"E173"),sQuery(id+"F0.wireOp",EDGE,"E174"),sQuery(id+"F0.wireOp",EDGE,"E175"),sQuery(id+"F0.wireOp",EDGE,"E176"),sQuery(id+"F0.wireOp",EDGE,"E177"),sQuery(id+"F0.wireOp",EDGE,"E178"),sQuery(id+"F0.wireOp",EDGE,"E179"),sQuery(id+"F0.wireOp",EDGE,"E180"),sQuery(id+"F0.wireOp",EDGE,"E181"),sQuery(id+"F0.wireOp",EDGE,"E182"),sQuery(id+"F0.wireOp",EDGE,"E183"),sQuery(id+"F0.wireOp",EDGE,"E184"),sQuery(id+"F0.wireOp",EDGE,"E185"),sQuery(id+"F0.wireOp",EDGE,"E186"),sQuery(id+"F0.wireOp",EDGE,"E187"),sQuery(id+"F0.wireOp",EDGE,"E188"),sQuery(id+"F0.wireOp",EDGE,"E189"),sQuery(id+"F0.wireOp",EDGE,"E190"),sQuery(id+"F0.wireOp",EDGE,"E191"),sQuery(id+"F0.wireOp",EDGE,"E192"),sQuery(id+"F0.wireOp",EDGE,"E193"),sQuery(id+"F0.wireOp",EDGE,"E194"),sQuery(id+"F0.wireOp",EDGE,"E195"),sQuery(id+"F0.wireOp",EDGE,"E196"),sQuery(id+"F0.wireOp",EDGE,"E197"),sQuery(id+"F0.wireOp",EDGE,"E198"),sQuery(id+"F0.wireOp",EDGE,"E199"),sQuery(id+"F0.wireOp",EDGE,"E200"),sQuery(id+"F0.wireOp",EDGE,"E201"),sQuery(id+"F0.wireOp",EDGE,"E202"),sQuery(id+"F0.wireOp",EDGE,"E203"),sQuery(id+"F0.wireOp",EDGE,"E204"),sQuery(id+"F0.wireOp",EDGE,"E205"),sQuery(id+"F0.wireOp",EDGE,"E206"),sQuery(id+"F0.wireOp",EDGE,"E207"),sQuery(id+"F0.wireOp",EDGE,"E208"),sQuery(id+"F0.wireOp",EDGE,"E209"),sQuery(id+"F0.wireOp",EDGE,"E210"),sQuery(id+"F0.wireOp",EDGE,"E211"),sQuery(id+"F0.wireOp",EDGE,"E212"),sQuery(id+"F0.wireOp",EDGE,"E213"),sQuery(id+"F0.wireOp",EDGE,"E214"),sQuery(id+"F0.wireOp",EDGE,"E215"),sQuery(id+"F0.wireOp",EDGE,"E216"),sQuery(id+"F0.wireOp",EDGE,"E217"),sQuery(id+"F0.wireOp",EDGE,"E218"),sQuery(id+"F0.wireOp",EDGE,"E219"),sQuery(id+"F0.wireOp",EDGE,"E220"),sQuery(id+"F0.wireOp",EDGE,"E221"),sQuery(id+"F0.wireOp",EDGE,"E222"),sQuery(id+"F0.wireOp",EDGE,"E223"),sQuery(id+"F0.wireOp",EDGE,"E224"),sQuery(id+"F0.wireOp",EDGE,"E225"),sQuery(id+"F0.wireOp",EDGE,"E226"),sQuery(id+"F0.wireOp",EDGE,"E227"),sQuery(id+"F0.wireOp",EDGE,"E228"),sQuery(id+"F0.wireOp",EDGE,"E229"),sQuery(id+"F0.wireOp",EDGE,"E230"),sQuery(id+"F0.wireOp",EDGE,"E231"),sQuery(id+"F0.wireOp",EDGE,"E232"),sQuery(id+"F0.wireOp",EDGE,"E233"),sQuery(id+"F0.wireOp",EDGE,"E234"),sQuery(id+"F0.wireOp",EDGE,"E235"),sQuery(id+"F0.wireOp",EDGE,"E236"),sQuery(id+"F0.wireOp",EDGE,"E237"),sQuery(id+"F0.wireOp",EDGE,"E238"),sQuery(id+"F0.wireOp",EDGE,"E239"),sQuery(id+"F0.wireOp",EDGE,"E240"),sQuery(id+"F0.wireOp",EDGE,"E241"),sQuery(id+"F0.wireOp",EDGE,"E242"),sQuery(id+"F0.wireOp",EDGE,"E243"),sQuery(id+"F0.wireOp",EDGE,"E244"),sQuery(id+"F0.wireOp",EDGE,"E245"),sQuery(id+"F0.wireOp",EDGE,"E246"),sQuery(id+"F0.wireOp",EDGE,"E247"),sQuery(id+"F0.wireOp",EDGE,"E248"),sQuery(id+"F0.wireOp",EDGE,"E249"),sQuery(id+"F0.wireOp",EDGE,"E250"),sQuery(id+"F0.wireOp",EDGE,"E251"),sQuery(id+"F0.wireOp",EDGE,"E252"),sQuery(id+"F0.wireOp",EDGE,"E253"),sQuery(id+"F0.wireOp",EDGE,"E254"),sQuery(id+"F0.wireOp",EDGE,"E255"),sQuery(id+"F0.wireOp",EDGE,"E256"),sQuery(id+"F0.wireOp",EDGE,"E257"),sQuery(id+"F0.wireOp",EDGE,"E258"),sQuery(id+"F0.wireOp",EDGE,"E259"),sQuery(id+"F0.wireOp",EDGE,"E260"),sQuery(id+"F0.wireOp",EDGE,"E261"),sQuery(id+"F0.wireOp",EDGE,"E262"),sQuery(id+"F0.wireOp",EDGE,"E263"),sQuery(id+"F0.wireOp",EDGE,"E264"),sQuery(id+"F0.wireOp",EDGE,"E265"),sQuery(id+"F0.wireOp",EDGE,"E266"),sQuery(id+"F0.wireOp",EDGE,"E267"),sQuery(id+"F0.wireOp",EDGE,"E268"),sQuery(id+"F0.wireOp",EDGE,"E269"),sQuery(id+"F0.wireOp",EDGE,"E270"),sQuery(id+"F0.wireOp",EDGE,"E271"),sQuery(id+"F0.wireOp",EDGE,"E272"),sQuery(id+"F0.wireOp",EDGE,"E273"),sQuery(id+"F0.wireOp",EDGE,"E274"),sQuery(id+"F0.wireOp",EDGE,"E275"),sQuery(id+"F0.wireOp",EDGE,"E276"),sQuery(id+"F0.wireOp",EDGE,"E277"),sQuery(id+"F0.wireOp",EDGE,"E278"),sQuery(id+"F0.wireOp",EDGE,"E279"),sQuery(id+"F0.wireOp",EDGE,"E280"),sQuery(id+"F0.wireOp",EDGE,"E281"),sQuery(id+"F0.wireOp",EDGE,"E282"),sQuery(id+"F0.wireOp",EDGE,"E283"),sQuery(id+"F0.wireOp",EDGE,"E284"),sQuery(id+"F0.wireOp",EDGE,"E285"),sQuery(id+"F0.wireOp",EDGE,"E286"),sQuery(id+"F0.wireOp",EDGE,"E287"),sQuery(id+"F0.wireOp",EDGE,"E288"),sQuery(id+"F0.wireOp",EDGE,"E289"),sQuery(id+"F0.wireOp",EDGE,"E290"),sQuery(id+"F0.wireOp",EDGE,"E291"),sQuery(id+"F0.wireOp",EDGE,"E292"),sQuery(id+"F0.wireOp",EDGE,"E293"),sQuery(id+"F0.wireOp",EDGE,"E294"),sQuery(id+"F0.wireOp",EDGE,"E295"),sQuery(id+"F0.wireOp",EDGE,"E296"),sQuery(id+"F0.wireOp",EDGE,"E297"),sQuery(id+"F0.wireOp",EDGE,"E298"),sQuery(id+"F0.wireOp",EDGE,"E299"),sQuery(id+"F0.wireOp",EDGE,"E300"),sQuery(id+"F0.wireOp",EDGE,"E301"),sQuery(id+"F0.wireOp",EDGE,"E302"),sQuery(id+"F0.wireOp",EDGE,"E303"),sQuery(id+"F0.wireOp",EDGE,"E304"),sQuery(id+"F0.wireOp",EDGE,"E305"),sQuery(id+"F0.wireOp",EDGE,"E306"),sQuery(id+"F0.wireOp",EDGE,"E307"),sQuery(id+"F0.wireOp",EDGE,"E308"),sQuery(id+"F0.wireOp",EDGE,"E309"),sQuery(id+"F0.wireOp",EDGE,"E310"),sQuery(id+"F0.wireOp",EDGE,"E311"),sQuery(id+"F0.wireOp",EDGE,"E312"),sQuery(id+"F0.wireOp",EDGE,"E313"),sQuery(id+"F0.wireOp",EDGE,"E314"),sQuery(id+"F0.wireOp",EDGE,"E315"),sQuery(id+"F0.wireOp",EDGE,"E316"),sQuery(id+"F0.wireOp",EDGE,"E317"),sQuery(id+"F0.wireOp",EDGE,"E318"),sQuery(id+"F0.wireOp",EDGE,"E319"),sQuery(id+"F0.wireOp",EDGE,"E320"),sQuery(id+"F0.wireOp",EDGE,"E321"),sQuery(id+"F0.wireOp",EDGE,"E322"),sQuery(id+"F0.wireOp",EDGE,"E323"),sQuery(id+"F0.wireOp",EDGE,"E324"),sQuery(id+"F0.wireOp",EDGE,"E325"),sQuery(id+"F0.wireOp",EDGE,"E326"),sQuery(id+"F0.wireOp",EDGE,"E327"),sQuery(id+"F0.wireOp",EDGE,"E328"),sQuery(id+"F0.wireOp",EDGE,"E329"),sQuery(id+"F0.wireOp",EDGE,"E330"),sQuery(id+"F0.wireOp",EDGE,"E331"),sQuery(id+"F0.wireOp",EDGE,"E332"),sQuery(id+"F0.wireOp",EDGE,"E333"),sQuery(id+"F0.wireOp",EDGE,"E334"),sQuery(id+"F0.wireOp",EDGE,"E335"),sQuery(id+"F0.wireOp",EDGE,"E336"),sQuery(id+"F0.wireOp",EDGE,"E337"),sQuery(id+"F0.wireOp",EDGE,"E338"),sQuery(id+"F0.wireOp",EDGE,"E339"),sQuery(id+"F0.wireOp",EDGE,"E340"),sQuery(id+"F0.wireOp",EDGE,"E341"),sQuery(id+"F0.wireOp",EDGE,"E342"),sQuery(id+"F0.wireOp",EDGE,"E343"),sQuery(id+"F0.wireOp",EDGE,"E344"),sQuery(id+"F0.wireOp",EDGE,"E345"),sQuery(id+"F0.wireOp",EDGE,"E346"),sQuery(id+"F0.wireOp",EDGE,"E347"),sQuery(id+"F0.wireOp",EDGE,"E348"),sQuery(id+"F0.wireOp",EDGE,"E349"),sQuery(id+"F0.wireOp",EDGE,"E350"),sQuery(id+"F0.wireOp",EDGE,"E351"),sQuery(id+"F0.wireOp",EDGE,"E352"),sQuery(id+"F0.wireOp",EDGE,"E353"),sQuery(id+"F0.wireOp",EDGE,"E354"),sQuery(id+"F0.wireOp",EDGE,"E355"),sQuery(id+"F0.wireOp",EDGE,"E356"),sQuery(id+"F0.wireOp",EDGE,"E357"),sQuery(id+"F0.wireOp",EDGE,"E358"),sQuery(id+"F0.wireOp",EDGE,"E359"),sQuery(id+"F0.wireOp",EDGE,"E360"),sQuery(id+"F0.wireOp",EDGE,"E361"),sQuery(id+"F0.wireOp",EDGE,"E362"),sQuery(id+"F0.wireOp",EDGE,"E363"),sQuery(id+"F0.wireOp",EDGE,"E364"),sQuery(id+"F0.wireOp",EDGE,"E365"),sQuery(id+"F0.wireOp",EDGE,"E366"),sQuery(id+"F0.wireOp",EDGE,"E367"),sQuery(id+"F0.wireOp",EDGE,"E368"),sQuery(id+"F0.wireOp",EDGE,"E369"),sQuery(id+"F0.wireOp",EDGE,"E370"),sQuery(id+"F0.wireOp",EDGE,"E371"),sQuery(id+"F0.wireOp",EDGE,"E372"),sQuery(id+"F0.wireOp",EDGE,"E373"),sQuery(id+"F0.wireOp",EDGE,"E374"),sQuery(id+"F0.wireOp",EDGE,"E375"),sQuery(id+"F0.wireOp",EDGE,"E376"),sQuery(id+"F0.wireOp",EDGE,"E377"),sQuery(id+"F0.wireOp",EDGE,"E378"),sQuery(id+"F0.wireOp",EDGE,"E379"),sQuery(id+"F0.wireOp",EDGE,"E380"),sQuery(id+"F0.wireOp",EDGE,"E381"),sQuery(id+"F0.wireOp",EDGE,"E382"),sQuery(id+"F0.wireOp",EDGE,"E383"),sQuery(id+"F0.wireOp",EDGE,"E384"),sQuery(id+"F0.wireOp",EDGE,"E385"),sQuery(id+"F0.wireOp",EDGE,"E386"),sQuery(id+"F0.wireOp",EDGE,"E387"),sQuery(id+"F0.wireOp",EDGE,"E388"),sQuery(id+"F0.wireOp",EDGE,"E389"),sQuery(id+"F0.wireOp",EDGE,"E390"),sQuery(id+"F0.wireOp",EDGE,"E391"),sQuery(id+"F0.wireOp",EDGE,"E392"),sQuery(id+"F0.wireOp",EDGE,"E393"),sQuery(id+"F0.wireOp",EDGE,"E394"),sQuery(id+"F0.wireOp",EDGE,"E395"),sQuery(id+"F0.wireOp",EDGE,"E396"),sQuery(id+"F0.wireOp",EDGE,"E397"),sQuery(id+"F0.wireOp",EDGE,"E398"),sQuery(id+"F0.wireOp",EDGE,"E399"),sQuery(id+"F0.wireOp",EDGE,"E400"),sQuery(id+"F0.wireOp",EDGE,"E401"),sQuery(id+"F0.wireOp",EDGE,"E402"),sQuery(id+"F0.wireOp",EDGE,"E403"),sQuery(id+"F0.wireOp",EDGE,"E404"),sQuery(id+"F0.wireOp",EDGE,"E405"),sQuery(id+"F0.wireOp",EDGE,"E406"),sQuery(id+"F0.wireOp",EDGE,"E407"),sQuery(id+"F0.wireOp",EDGE,"E408"),sQuery(id+"F0.wireOp",EDGE,"E409"),sQuery(id+"F0.wireOp",EDGE,"E410"),sQuery(id+"F0.wireOp",EDGE,"E411"),sQuery(id+"F0.wireOp",EDGE,"E412"),sQuery(id+"F0.wireOp",EDGE,"E413"),sQuery(id+"F0.wireOp",EDGE,"E414")])],"isStart":true});
            var sketch = newSketch(context, id + "F2", { "sketchPlane" : qUnion([Q0])});
            skCircle(sketch, "E415", {"center": v(-15.24, 0) * mm, "radius": 1.9 * mm});
            skCircle(sketch, "E416.1.0", {"center": v(7.62, -13.2) * mm, "radius": 1.9 * mm});
            skCircle(sketch, "E416.2.0", {"center": v(7.62, 13.2) * mm, "radius": 1.9 * mm});
            skPoint(sketch, "E416.center", {"position": v(0, 0) * mm});
            skSolve(sketch);
        }
        {
            var Q0;
            Q0=makeQuery(id+"F2.imprint","IMPRINT",FACE,{"disambiguationData":[TD([[makeQuery(id+"F2.imprint","IMPRINT",EDGE,{"derivedFrom":sQuery(id+"F2.wireOp",EDGE,"E416.2.0")}),1.0]])]});
            var Q1;
            Q1=makeQuery(id+"F2.imprint","IMPRINT",FACE,{"disambiguationData":[TD([[makeQuery(id+"F2.imprint","IMPRINT",EDGE,{"derivedFrom":sQuery(id+"F2.wireOp",EDGE,"E416.1.0")}),1.0]])]});
            var Q2;
            Q2=makeQuery(id+"F2.imprint","IMPRINT",FACE,{"disambiguationData":[TD([[makeQuery(id+"F2.imprint","IMPRINT",EDGE,{"derivedFrom":sQuery(id+"F2.wireOp",EDGE,"E415")}),1.0]])]});
            extrude(context, id + "F3", {"entities" : qUnion([Q0, Q1, Q2]), "operationType" : NewBodyOperationType.REMOVE, "endBound" : BoundingType.THROUGH_ALL, "oppositeDirection" : true, "depth" : 25.4 * mm, "offsetDistance" : 25.4 * mm});
        }
    });
